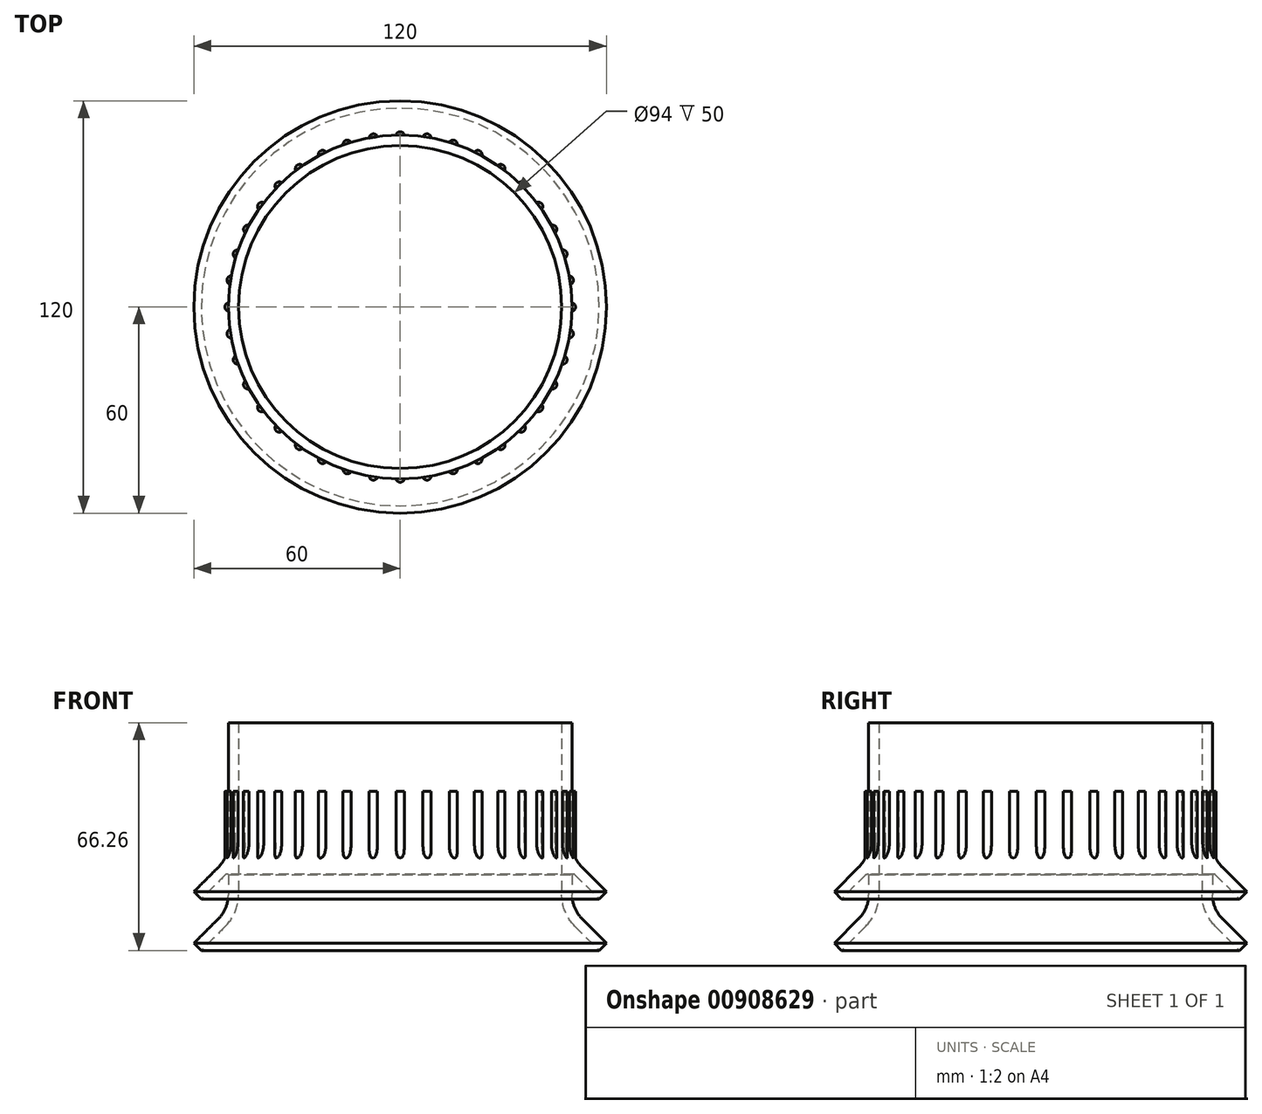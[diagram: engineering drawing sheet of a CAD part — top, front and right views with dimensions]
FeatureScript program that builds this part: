
annotation { "Feature Type Name" : "Feature", "Feature Type Description" : "" }
export const myFeature = defineFeature(function(context is Context, id is Id, definition is map)
    precondition{}
    {
        {
            var Q0;
            Q0=qCreatedBy(makeId("Front.planeOp"),FACE);
            var sketch = newSketch(context, id + "F0", { "sketchPlane" : qUnion([Q0])});
            skLineSegment(sketch, "E0", {"start": v(52.93, -7.07) * mm, "end": v(60, -14.14) * mm});
            skArc(sketch, "E1", {"start": v(50, 0) * mm, "mid": v(50.76, -3.83) * mm, "end": v(52.93, -7.07) * mm});
            skLineSegment(sketch, "E2.0", {"start": v(47, 0) * mm, "end": v(47, 50) * mm});
            skArc(sketch, "E3.0", {"start": v(47, 0) * mm, "mid": v(47.99, -4.97) * mm, "end": v(50.8, -9.2) * mm});
            skLineSegment(sketch, "E4.0", {"start": v(50.8, -9.2) * mm, "end": v(57.88, -16.26) * mm});
            skLineSegment(sketch, "E5", {"start": v(57.88, -16.26) * mm, "end": v(60, -14.14) * mm});
            skLineSegment(sketch, "E6", {"start": v(50, 50) * mm, "end": v(47, 50) * mm});
            skLineSegment(sketch, "E7", {"start": v(0, 0) * mm, "end": v(0, 52.3) * mm});
            skArc(sketch, "E8.1.0.0", {"start": v(50, 15) * mm, "mid": v(50.76, 11.17) * mm, "end": v(52.93, 7.93) * mm});
            skLineSegment(sketch, "E8.1.0.2", {"start": v(52.93, 7.93) * mm, "end": v(60, 0.86) * mm});
            skLineSegment(sketch, "E8.1.0.3", {"start": v(50.8, 5.8) * mm, "end": v(57.88, -1.26) * mm});
            skLineSegment(sketch, "E8.1.0.4", {"start": v(57.88, -1.26) * mm, "end": v(60, 0.86) * mm});
            skLineSegment(sketch, "E8.direction1", {"start": v(57.88, -16.26) * mm, "end": v(57.88, -1.26) * mm, "construction": true});
            skLineSegment(sketch, "E9", {"start": v(50, 50) * mm, "end": v(50, 15) * mm});
            skLineSegment(sketch, "E10", {"start": v(50, 0) * mm, "end": v(50, 9.71) * mm, "construction": true});
            skLineSegment(sketch, "E11", {"start": v(50, 5.8) * mm, "end": v(50, 0) * mm});
            skArc(sketch, "E12", {"start": v(50.8, 5.8) * mm, "mid": v(50.4, 5.97) * mm, "end": v(50, 5.8) * mm});
            skArc(sketch, "E13", {"start": v(50, 50) * mm, "mid": v(51.25, 48.75) * mm, "end": v(50, 47.5) * mm});
            skSolve(sketch);
        }
        {
            var Q0;
            Q0=makeQuery(id+"F0.imprint","IMPRINT",FACE,{"disambiguationData":[TD([[makeQuery(id+"F0.imprint","IMPRINT",EDGE,{"derivedFrom":sQuery(id+"F0.wireOp",EDGE,"E0")}),-1.0]])]});
            var Q1;
            Q1=sQuery(id+"F0.wireOp",EDGE,"E8.1.0.3");
            var Q2;
            Q2=sQuery(id+"F0.wireOp",EDGE,"E8.1.0.0");
            var Q3;
            Q3=sQuery(id+"F0.wireOp",EDGE,"E8.1.0.2");
            var Q4;
            Q4=sQuery(id+"F0.wireOp",EDGE,"E8.1.0.4");
            var Q5;
            Q5=sQuery(id+"F0.wireOp",EDGE,"E1");
            var Q6;
            Q6=sQuery(id+"F0.wireOp",EDGE,"E3.0");
            var Q7;
            Q7=sQuery(id+"F0.wireOp",EDGE,"E4.0");
            var Q8;
            Q8=sQuery(id+"F0.wireOp",EDGE,"E0");
            var Q9;
            Q9=sQuery(id+"F0.wireOp",EDGE,"E5");
            var Q10;
            Q10=sQuery(id+"F0.wireOp",EDGE,"IlPTqso3-wrpj-7sc2-H875-co7WG8RhS1iU");
            var Q11;
            Q11=sQuery(id+"F0.wireOp",EDGE,"E2.0");
            var Q12;
            Q12=sQuery(id+"F0.wireOp",EDGE,"E6");
            var Q13;
            Q13=sQuery(id+"F0.wireOp",EDGE,"E12");
            var Q14;
            Q14=sQuery(id+"F0.wireOp",EDGE,"E9");
            var Q15;
            Q15=sQuery(id+"F0.wireOp",EDGE,"E11");
            var Q16;
            Q16=sQuery(id+"F0.wireOp",EDGE,"E7");
            revolve(context, id + "F1", {"surfaceOperationType" : NewSurfaceOperationType.NEW, "entities" : qUnion([Q0]), "surfaceEntities" : qUnion([Q1, Q2, Q3, Q4, Q5, Q6, Q7, Q8, Q9, Q10, Q11, Q12, Q13, Q14, Q15]), "axis" : qUnion([Q16]), "revolveType" : RevolveType.FULL});
        }
        {
            var Q0;
            Q0=qCreatedBy(makeId("Top.planeOp"),FACE);
            cPlane(context, id + "F2", {"entities" : qUnion([Q0]), "cplaneType" : CPlaneType.OFFSET, "offset" : 30 * mm, "width" : 150 * mm, "height" : 150 * mm});
        }
        {
            var Q0;
            Q0=qCreatedBy(id+"F2.planeOp",FACE);
            var sketch = newSketch(context, id + "F3", { "sketchPlane" : qUnion([Q0])});
            skCircle(sketch, "E14", {"center": v(0, 0) * mm, "radius": 50 * mm});
            skArc(sketch, "E15", {"start": v(1.23, 49.98) * mm, "mid": v(0, 51) * mm, "end": v(-1.23, 49.98) * mm});
            skArc(sketch, "E16.1.0", {"start": v(-6.6, 49.56) * mm, "mid": v(-7.98, 50.37) * mm, "end": v(-9.03, 49.18) * mm});
            skArc(sketch, "E17.3.2.0", {"start": v(-14.28, 47.92) * mm, "mid": v(-15.76, 48.5) * mm, "end": v(-16.61, 47.16) * mm});
            skArc(sketch, "E17.3.3.0", {"start": v(-21.6, 45.1) * mm, "mid": v(-23.15, 45.44) * mm, "end": v(-23.79, 43.98) * mm});
            skArc(sketch, "E17.3.4.0", {"start": v(-28.39, 41.16) * mm, "mid": v(-29.98, 41.26) * mm, "end": v(-30.37, 39.72) * mm});
            skArc(sketch, "E17.3.5.0", {"start": v(-34.48, 36.21) * mm, "mid": v(-36.06, 36.06) * mm, "end": v(-36.21, 34.48) * mm});
            skArc(sketch, "E17.3.6.0", {"start": v(-39.72, 30.37) * mm, "mid": v(-41.26, 29.98) * mm, "end": v(-41.16, 28.39) * mm});
            skArc(sketch, "E17.3.7.0", {"start": v(-43.98, 23.79) * mm, "mid": v(-45.44, 23.15) * mm, "end": v(-45.1, 21.6) * mm});
            skArc(sketch, "E17.3.8.0", {"start": v(-47.16, 16.61) * mm, "mid": v(-48.5, 15.76) * mm, "end": v(-47.92, 14.28) * mm});
            skArc(sketch, "E17.3.9.0", {"start": v(-49.18, 9.03) * mm, "mid": v(-50.37, 7.98) * mm, "end": v(-49.56, 6.6) * mm});
            skArc(sketch, "E17.3.10.0", {"start": v(-49.98, 1.23) * mm, "mid": v(-51, 0) * mm, "end": v(-49.98, -1.23) * mm});
            skArc(sketch, "E17.3.11.0", {"start": v(-49.56, -6.6) * mm, "mid": v(-50.37, -7.98) * mm, "end": v(-49.18, -9.03) * mm});
            skArc(sketch, "E17.3.12.0", {"start": v(-47.92, -14.28) * mm, "mid": v(-48.5, -15.76) * mm, "end": v(-47.16, -16.61) * mm});
            skArc(sketch, "E17.3.13.0", {"start": v(-45.1, -21.6) * mm, "mid": v(-45.44, -23.15) * mm, "end": v(-43.98, -23.79) * mm});
            skArc(sketch, "E17.3.14.0", {"start": v(-41.16, -28.39) * mm, "mid": v(-41.26, -29.98) * mm, "end": v(-39.72, -30.37) * mm});
            skArc(sketch, "E17.3.15.0", {"start": v(-36.21, -34.48) * mm, "mid": v(-36.06, -36.06) * mm, "end": v(-34.48, -36.21) * mm});
            skArc(sketch, "E17.3.16.0", {"start": v(-30.37, -39.72) * mm, "mid": v(-29.98, -41.26) * mm, "end": v(-28.39, -41.16) * mm});
            skArc(sketch, "E17.3.17.0", {"start": v(-23.79, -43.98) * mm, "mid": v(-23.15, -45.44) * mm, "end": v(-21.6, -45.1) * mm});
            skArc(sketch, "E17.3.18.0", {"start": v(-16.61, -47.16) * mm, "mid": v(-15.76, -48.5) * mm, "end": v(-14.28, -47.92) * mm});
            skArc(sketch, "E17.3.19.0", {"start": v(-9.03, -49.18) * mm, "mid": v(-7.98, -50.37) * mm, "end": v(-6.6, -49.56) * mm});
            skArc(sketch, "E18.3.20.0", {"start": v(-1.23, -49.98) * mm, "mid": v(0, -51) * mm, "end": v(1.23, -49.98) * mm});
            skArc(sketch, "E18.3.21.0", {"start": v(6.6, -49.56) * mm, "mid": v(7.98, -50.37) * mm, "end": v(9.03, -49.18) * mm});
            skArc(sketch, "E18.3.22.0", {"start": v(14.28, -47.92) * mm, "mid": v(15.76, -48.5) * mm, "end": v(16.61, -47.16) * mm});
            skArc(sketch, "E18.3.23.0", {"start": v(21.6, -45.1) * mm, "mid": v(23.15, -45.44) * mm, "end": v(23.79, -43.98) * mm});
            skArc(sketch, "E18.3.24.0", {"start": v(28.39, -41.16) * mm, "mid": v(29.98, -41.26) * mm, "end": v(30.37, -39.72) * mm});
            skArc(sketch, "E18.3.25.0", {"start": v(34.48, -36.21) * mm, "mid": v(36.06, -36.06) * mm, "end": v(36.21, -34.48) * mm});
            skArc(sketch, "E18.3.26.0", {"start": v(39.72, -30.37) * mm, "mid": v(41.26, -29.98) * mm, "end": v(41.16, -28.39) * mm});
            skArc(sketch, "E18.3.27.0", {"start": v(43.98, -23.79) * mm, "mid": v(45.44, -23.15) * mm, "end": v(45.1, -21.6) * mm});
            skArc(sketch, "E18.3.28.0", {"start": v(47.16, -16.61) * mm, "mid": v(48.5, -15.76) * mm, "end": v(47.92, -14.28) * mm});
            skArc(sketch, "E18.3.29.0", {"start": v(49.18, -9.03) * mm, "mid": v(50.37, -7.98) * mm, "end": v(49.56, -6.6) * mm});
            skArc(sketch, "E19.3.30.0", {"start": v(49.98, -1.23) * mm, "mid": v(51, 0) * mm, "end": v(49.98, 1.23) * mm});
            skArc(sketch, "E19.3.31.0", {"start": v(49.56, 6.6) * mm, "mid": v(50.37, 7.98) * mm, "end": v(49.18, 9.03) * mm});
            skArc(sketch, "E19.3.32.0", {"start": v(47.92, 14.28) * mm, "mid": v(48.5, 15.76) * mm, "end": v(47.16, 16.61) * mm});
            skArc(sketch, "E19.3.33.0", {"start": v(45.1, 21.6) * mm, "mid": v(45.44, 23.15) * mm, "end": v(43.98, 23.79) * mm});
            skArc(sketch, "E19.3.34.0", {"start": v(41.16, 28.39) * mm, "mid": v(41.26, 29.98) * mm, "end": v(39.72, 30.37) * mm});
            skArc(sketch, "E19.3.35.0", {"start": v(36.21, 34.48) * mm, "mid": v(36.06, 36.06) * mm, "end": v(34.48, 36.21) * mm});
            skArc(sketch, "E19.3.36.0", {"start": v(30.37, 39.72) * mm, "mid": v(29.98, 41.26) * mm, "end": v(28.39, 41.16) * mm});
            skArc(sketch, "E19.3.37.0", {"start": v(23.79, 43.98) * mm, "mid": v(23.15, 45.44) * mm, "end": v(21.6, 45.1) * mm});
            skArc(sketch, "E19.3.38.0", {"start": v(16.61, 47.16) * mm, "mid": v(15.76, 48.5) * mm, "end": v(14.28, 47.92) * mm});
            skArc(sketch, "E19.3.39.0", {"start": v(9.03, 49.18) * mm, "mid": v(7.98, 50.37) * mm, "end": v(6.6, 49.56) * mm});
            skSolve(sketch);
        }
        {
            var Q0;
            {var subQ0=sQuery(id+"F3.wireOp",EDGE,"E15");Q0=makeQuery(id+"F3.imprint","IMPRINT",FACE,{"disambiguationData":[TD([[makeQuery(id+"F3.imprint","IMPRINT",EDGE,{"derivedFrom":subQ0}),1.0]])]});}
            var Q1;
            {var subQ0=sQuery(id+"F3.wireOp",EDGE,"E19.3.39.0");Q1=makeQuery(id+"F3.imprint","IMPRINT",FACE,{"disambiguationData":[TD([[makeQuery(id+"F3.imprint","IMPRINT",EDGE,{"derivedFrom":subQ0}),1.0]])]});}
            var Q2;
            {var subQ0=sQuery(id+"F3.wireOp",EDGE,"E19.3.38.0");Q2=makeQuery(id+"F3.imprint","IMPRINT",FACE,{"disambiguationData":[TD([[makeQuery(id+"F3.imprint","IMPRINT",EDGE,{"derivedFrom":subQ0}),1.0]])]});}
            var Q3;
            {var subQ0=sQuery(id+"F3.wireOp",EDGE,"E19.3.37.0");Q3=makeQuery(id+"F3.imprint","IMPRINT",FACE,{"disambiguationData":[TD([[makeQuery(id+"F3.imprint","IMPRINT",EDGE,{"derivedFrom":subQ0}),1.0]])]});}
            var Q4;
            {var subQ0=sQuery(id+"F3.wireOp",EDGE,"E19.3.36.0");Q4=makeQuery(id+"F3.imprint","IMPRINT",FACE,{"disambiguationData":[TD([[makeQuery(id+"F3.imprint","IMPRINT",EDGE,{"derivedFrom":subQ0}),1.0]])]});}
            var Q5;
            {var subQ0=sQuery(id+"F3.wireOp",EDGE,"E19.3.35.0");Q5=makeQuery(id+"F3.imprint","IMPRINT",FACE,{"disambiguationData":[TD([[makeQuery(id+"F3.imprint","IMPRINT",EDGE,{"derivedFrom":subQ0}),1.0]])]});}
            var Q6;
            {var subQ0=sQuery(id+"F3.wireOp",EDGE,"E19.3.34.0");Q6=makeQuery(id+"F3.imprint","IMPRINT",FACE,{"disambiguationData":[TD([[makeQuery(id+"F3.imprint","IMPRINT",EDGE,{"derivedFrom":subQ0}),1.0]])]});}
            var Q7;
            {var subQ0=sQuery(id+"F3.wireOp",EDGE,"E19.3.33.0");Q7=makeQuery(id+"F3.imprint","IMPRINT",FACE,{"disambiguationData":[TD([[makeQuery(id+"F3.imprint","IMPRINT",EDGE,{"derivedFrom":subQ0}),1.0]])]});}
            var Q8;
            {var subQ0=sQuery(id+"F3.wireOp",EDGE,"E19.3.32.0");Q8=makeQuery(id+"F3.imprint","IMPRINT",FACE,{"disambiguationData":[TD([[makeQuery(id+"F3.imprint","IMPRINT",EDGE,{"derivedFrom":subQ0}),1.0]])]});}
            var Q9;
            {var subQ0=sQuery(id+"F3.wireOp",EDGE,"E19.3.31.0");Q9=makeQuery(id+"F3.imprint","IMPRINT",FACE,{"disambiguationData":[TD([[makeQuery(id+"F3.imprint","IMPRINT",EDGE,{"derivedFrom":subQ0}),1.0]])]});}
            var Q10;
            {var subQ0=sQuery(id+"F3.wireOp",EDGE,"E19.3.30.0");Q10=makeQuery(id+"F3.imprint","IMPRINT",FACE,{"disambiguationData":[TD([[makeQuery(id+"F3.imprint","IMPRINT",EDGE,{"derivedFrom":subQ0}),1.0]])]});}
            var Q11;
            {var subQ0=sQuery(id+"F3.wireOp",EDGE,"E18.3.29.0");Q11=makeQuery(id+"F3.imprint","IMPRINT",FACE,{"disambiguationData":[TD([[makeQuery(id+"F3.imprint","IMPRINT",EDGE,{"derivedFrom":subQ0}),1.0]])]});}
            var Q12;
            {var subQ0=sQuery(id+"F3.wireOp",EDGE,"E18.3.28.0");Q12=makeQuery(id+"F3.imprint","IMPRINT",FACE,{"disambiguationData":[TD([[makeQuery(id+"F3.imprint","IMPRINT",EDGE,{"derivedFrom":subQ0}),1.0]])]});}
            var Q13;
            {var subQ0=sQuery(id+"F3.wireOp",EDGE,"E18.3.27.0");Q13=makeQuery(id+"F3.imprint","IMPRINT",FACE,{"disambiguationData":[TD([[makeQuery(id+"F3.imprint","IMPRINT",EDGE,{"derivedFrom":subQ0}),1.0]])]});}
            var Q14;
            {var subQ0=sQuery(id+"F3.wireOp",EDGE,"E18.3.26.0");Q14=makeQuery(id+"F3.imprint","IMPRINT",FACE,{"disambiguationData":[TD([[makeQuery(id+"F3.imprint","IMPRINT",EDGE,{"derivedFrom":subQ0}),1.0]])]});}
            var Q15;
            {var subQ0=sQuery(id+"F3.wireOp",EDGE,"E18.3.25.0");Q15=makeQuery(id+"F3.imprint","IMPRINT",FACE,{"disambiguationData":[TD([[makeQuery(id+"F3.imprint","IMPRINT",EDGE,{"derivedFrom":subQ0}),1.0]])]});}
            var Q16;
            {var subQ0=sQuery(id+"F3.wireOp",EDGE,"E18.3.24.0");Q16=makeQuery(id+"F3.imprint","IMPRINT",FACE,{"disambiguationData":[TD([[makeQuery(id+"F3.imprint","IMPRINT",EDGE,{"derivedFrom":subQ0}),1.0]])]});}
            var Q17;
            {var subQ0=sQuery(id+"F3.wireOp",EDGE,"E18.3.23.0");Q17=makeQuery(id+"F3.imprint","IMPRINT",FACE,{"disambiguationData":[TD([[makeQuery(id+"F3.imprint","IMPRINT",EDGE,{"derivedFrom":subQ0}),1.0]])]});}
            var Q18;
            {var subQ0=sQuery(id+"F3.wireOp",EDGE,"E18.3.22.0");Q18=makeQuery(id+"F3.imprint","IMPRINT",FACE,{"disambiguationData":[TD([[makeQuery(id+"F3.imprint","IMPRINT",EDGE,{"derivedFrom":subQ0}),1.0]])]});}
            var Q19;
            {var subQ0=sQuery(id+"F3.wireOp",EDGE,"E18.3.21.0");Q19=makeQuery(id+"F3.imprint","IMPRINT",FACE,{"disambiguationData":[TD([[makeQuery(id+"F3.imprint","IMPRINT",EDGE,{"derivedFrom":subQ0}),1.0]])]});}
            var Q20;
            {var subQ0=sQuery(id+"F3.wireOp",EDGE,"E18.3.20.0");Q20=makeQuery(id+"F3.imprint","IMPRINT",FACE,{"disambiguationData":[TD([[makeQuery(id+"F3.imprint","IMPRINT",EDGE,{"derivedFrom":subQ0}),1.0]])]});}
            var Q21;
            {var subQ0=sQuery(id+"F3.wireOp",EDGE,"E17.3.19.0");Q21=makeQuery(id+"F3.imprint","IMPRINT",FACE,{"disambiguationData":[TD([[makeQuery(id+"F3.imprint","IMPRINT",EDGE,{"derivedFrom":subQ0}),1.0]])]});}
            var Q22;
            {var subQ0=sQuery(id+"F3.wireOp",EDGE,"E17.3.18.0");Q22=makeQuery(id+"F3.imprint","IMPRINT",FACE,{"disambiguationData":[TD([[makeQuery(id+"F3.imprint","IMPRINT",EDGE,{"derivedFrom":subQ0}),1.0]])]});}
            var Q23;
            {var subQ0=sQuery(id+"F3.wireOp",EDGE,"E17.3.17.0");Q23=makeQuery(id+"F3.imprint","IMPRINT",FACE,{"disambiguationData":[TD([[makeQuery(id+"F3.imprint","IMPRINT",EDGE,{"derivedFrom":subQ0}),1.0]])]});}
            var Q24;
            {var subQ0=sQuery(id+"F3.wireOp",EDGE,"E17.3.15.0");Q24=makeQuery(id+"F3.imprint","IMPRINT",FACE,{"disambiguationData":[TD([[makeQuery(id+"F3.imprint","IMPRINT",EDGE,{"derivedFrom":subQ0}),1.0]])]});}
            var Q25;
            {var subQ0=sQuery(id+"F3.wireOp",EDGE,"E17.3.16.0");Q25=makeQuery(id+"F3.imprint","IMPRINT",FACE,{"disambiguationData":[TD([[makeQuery(id+"F3.imprint","IMPRINT",EDGE,{"derivedFrom":subQ0}),1.0]])]});}
            var Q26;
            {var subQ0=sQuery(id+"F3.wireOp",EDGE,"E17.3.14.0");Q26=makeQuery(id+"F3.imprint","IMPRINT",FACE,{"disambiguationData":[TD([[makeQuery(id+"F3.imprint","IMPRINT",EDGE,{"derivedFrom":subQ0}),1.0]])]});}
            var Q27;
            {var subQ0=sQuery(id+"F3.wireOp",EDGE,"E17.3.13.0");Q27=makeQuery(id+"F3.imprint","IMPRINT",FACE,{"disambiguationData":[TD([[makeQuery(id+"F3.imprint","IMPRINT",EDGE,{"derivedFrom":subQ0}),1.0]])]});}
            var Q28;
            {var subQ0=sQuery(id+"F3.wireOp",EDGE,"E17.3.12.0");Q28=makeQuery(id+"F3.imprint","IMPRINT",FACE,{"disambiguationData":[TD([[makeQuery(id+"F3.imprint","IMPRINT",EDGE,{"derivedFrom":subQ0}),1.0]])]});}
            var Q29;
            {var subQ0=sQuery(id+"F3.wireOp",EDGE,"E17.3.11.0");Q29=makeQuery(id+"F3.imprint","IMPRINT",FACE,{"disambiguationData":[TD([[makeQuery(id+"F3.imprint","IMPRINT",EDGE,{"derivedFrom":subQ0}),1.0]])]});}
            var Q30;
            {var subQ0=sQuery(id+"F3.wireOp",EDGE,"E17.3.10.0");Q30=makeQuery(id+"F3.imprint","IMPRINT",FACE,{"disambiguationData":[TD([[makeQuery(id+"F3.imprint","IMPRINT",EDGE,{"derivedFrom":subQ0}),1.0]])]});}
            var Q31;
            {var subQ0=sQuery(id+"F3.wireOp",EDGE,"E17.3.9.0");Q31=makeQuery(id+"F3.imprint","IMPRINT",FACE,{"disambiguationData":[TD([[makeQuery(id+"F3.imprint","IMPRINT",EDGE,{"derivedFrom":subQ0}),1.0]])]});}
            var Q32;
            {var subQ0=sQuery(id+"F3.wireOp",EDGE,"E17.3.8.0");Q32=makeQuery(id+"F3.imprint","IMPRINT",FACE,{"disambiguationData":[TD([[makeQuery(id+"F3.imprint","IMPRINT",EDGE,{"derivedFrom":subQ0}),1.0]])]});}
            var Q33;
            {var subQ0=sQuery(id+"F3.wireOp",EDGE,"E17.3.7.0");Q33=makeQuery(id+"F3.imprint","IMPRINT",FACE,{"disambiguationData":[TD([[makeQuery(id+"F3.imprint","IMPRINT",EDGE,{"derivedFrom":subQ0}),1.0]])]});}
            var Q34;
            {var subQ0=sQuery(id+"F3.wireOp",EDGE,"E16.1.0");Q34=makeQuery(id+"F3.imprint","IMPRINT",FACE,{"disambiguationData":[TD([[makeQuery(id+"F3.imprint","IMPRINT",EDGE,{"derivedFrom":subQ0}),1.0]])]});}
            var Q35;
            {var subQ0=sQuery(id+"F3.wireOp",EDGE,"E17.3.2.0");Q35=makeQuery(id+"F3.imprint","IMPRINT",FACE,{"disambiguationData":[TD([[makeQuery(id+"F3.imprint","IMPRINT",EDGE,{"derivedFrom":subQ0}),1.0]])]});}
            var Q36;
            {var subQ0=sQuery(id+"F3.wireOp",EDGE,"E17.3.3.0");Q36=makeQuery(id+"F3.imprint","IMPRINT",FACE,{"disambiguationData":[TD([[makeQuery(id+"F3.imprint","IMPRINT",EDGE,{"derivedFrom":subQ0}),1.0]])]});}
            var Q37;
            {var subQ0=sQuery(id+"F3.wireOp",EDGE,"E17.3.4.0");Q37=makeQuery(id+"F3.imprint","IMPRINT",FACE,{"disambiguationData":[TD([[makeQuery(id+"F3.imprint","IMPRINT",EDGE,{"derivedFrom":subQ0}),1.0]])]});}
            var Q38;
            {var subQ0=sQuery(id+"F3.wireOp",EDGE,"E17.3.5.0");Q38=makeQuery(id+"F3.imprint","IMPRINT",FACE,{"disambiguationData":[TD([[makeQuery(id+"F3.imprint","IMPRINT",EDGE,{"derivedFrom":subQ0}),1.0]])]});}
            var Q39;
            {var subQ0=sQuery(id+"F3.wireOp",EDGE,"E17.3.6.0");Q39=makeQuery(id+"F3.imprint","IMPRINT",FACE,{"disambiguationData":[TD([[makeQuery(id+"F3.imprint","IMPRINT",EDGE,{"derivedFrom":subQ0}),1.0]])]});}
            extrude(context, id + "F4", {"entities" : qUnion([Q0, Q1, Q2, Q3, Q4, Q5, Q6, Q7, Q8, Q9, Q10, Q11, Q12, Q13, Q14, Q15, Q16, Q17, Q18, Q19, Q20, Q21, Q22, Q23, Q24, Q25, Q26, Q27, Q28, Q29, Q30, Q31, Q32, Q33, Q34, Q35, Q36, Q37, Q38, Q39]), "operationType" : NewBodyOperationType.ADD, "endBound" : BoundingType.UP_TO_NEXT, "oppositeDirection" : true, "depth" : 30 * mm, "offsetDistance" : 25 * mm});
        }
    });
